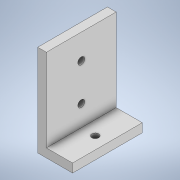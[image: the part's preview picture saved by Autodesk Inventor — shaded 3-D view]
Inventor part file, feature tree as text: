
AUTODESK INVENTOR PART (.ipt)
format: ipt  version: 2021 (Build 250183000, 183)  size: 113,152 bytes
history: native  units: mm
features: extrude x3, sketch x3, pattern_linear x1
ambient origin geometry x8: Origin, YZ Plane, XZ Plane, XY Plane, X Axis, Y Axis, Z Axis, Center Point
bodies: Solid1 (feature_tree)
feature tree (7):
  extrude  "Extrusion1"  Depth=10.0mm
  extrude  "Extrusion2"  Depth=30.0mm
  pattern_linear  "Rectangular Pattern1"  Count1=4  [1 undecoded]
  extrude  "Extrusion3"  Depth=80.0mm TaperAngle=0.0deg
  sketch  "Sketch1"  dims[d0=105.0mm d1=10.0mm]
  sketch  "Sketch2"  dims[d2=95.0mm d3=30.0mm]
  sketch  "Sketch3"  dims[d4=10.0mm d5=40.0mm d6=80.0mm d7=0.0mm d8=8.0mm d9=10.0mm d10=0.0mm d11=20.0mm d13=42.5mm d14=8.0mm d15=10.0mm d16=0.0mm]
note: 1 required parameter value undecoded (feature->parameter linkage not recoverable at this tier; creation-order binding heuristic only, values carry confidence <= 0.55)
